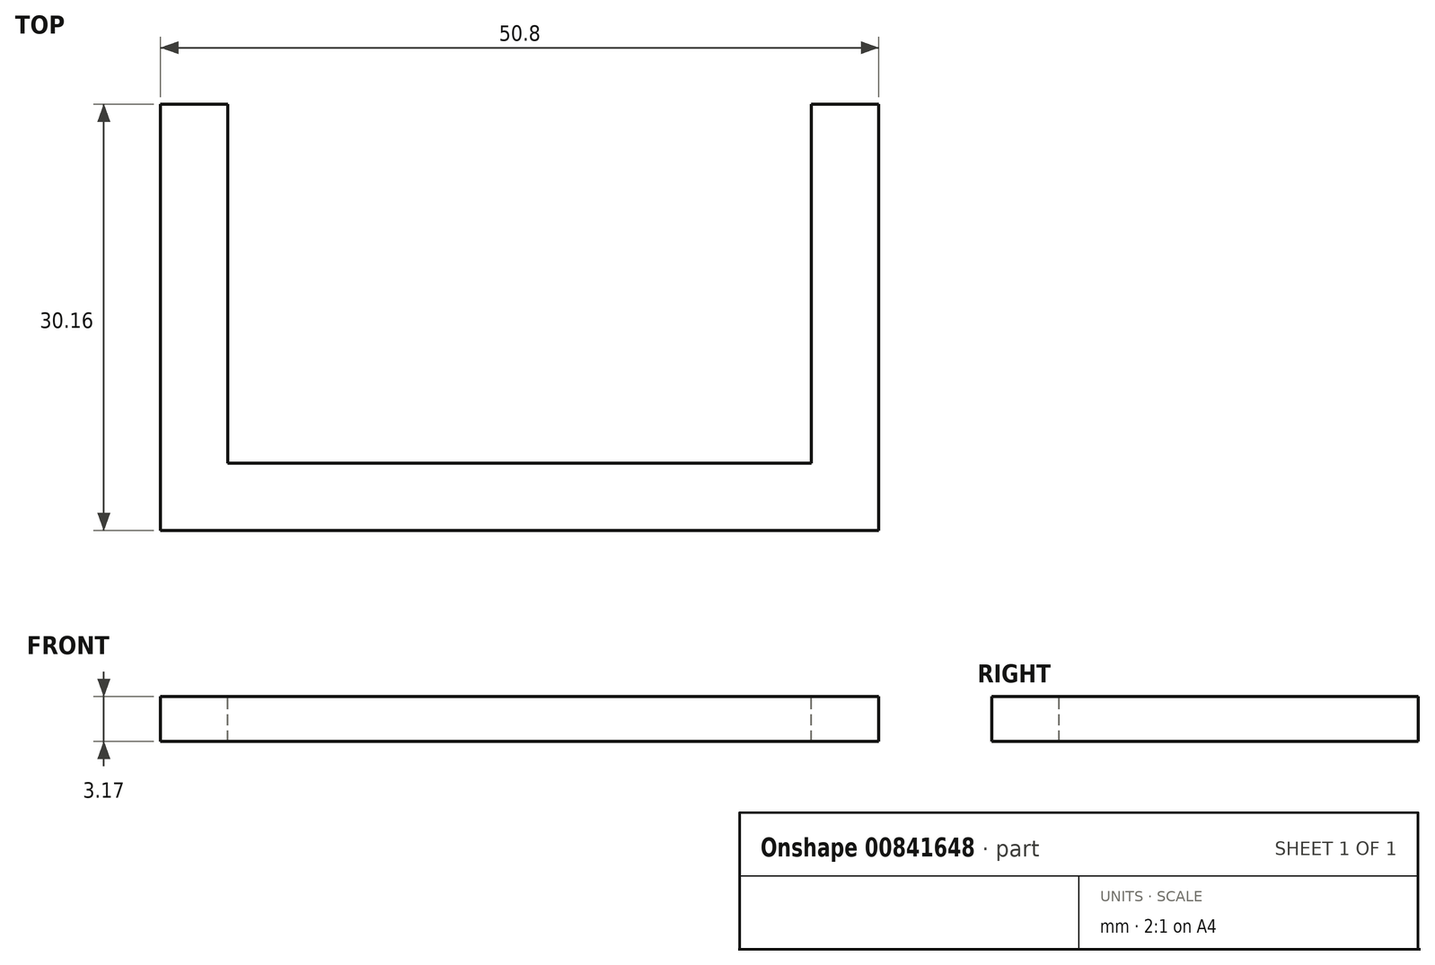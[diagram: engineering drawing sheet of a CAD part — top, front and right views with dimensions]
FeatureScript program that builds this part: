
annotation { "Feature Type Name" : "Feature", "Feature Type Description" : "" }
export const myFeature = defineFeature(function(context is Context, id is Id, definition is map)
    precondition{}
    {
        {
            var Q0;
            Q0=qCreatedBy(makeId("Top.planeOp"),FACE);
            var sketch = newSketch(context, id + "F0", { "sketchPlane" : qUnion([Q0])});
            skLineSegment(sketch, "E0.top", {"start": v(-34.87, -8.74) * mm, "end": v(6.4, -8.74) * mm});
            skLineSegment(sketch, "E0.left", {"start": v(-34.87, 16.66) * mm, "end": v(-34.87, -8.74) * mm});
            skLineSegment(sketch, "E0.right", {"start": v(6.4, 16.66) * mm, "end": v(6.4, -8.74) * mm});
            skLineSegment(sketch, "E1.top", {"start": v(-39.63, -13.5) * mm, "end": v(11.17, -13.5) * mm});
            skLineSegment(sketch, "E1.left", {"start": v(-39.63, 16.66) * mm, "end": v(-39.63, -13.5) * mm});
            skLineSegment(sketch, "E1.right", {"start": v(11.17, 16.66) * mm, "end": v(11.17, -13.5) * mm});
            skLineSegment(sketch, "E2", {"start": v(-39.63, 16.66) * mm, "end": v(-34.87, 16.66) * mm});
            skLineSegment(sketch, "E3", {"start": v(6.4, 16.66) * mm, "end": v(11.17, 16.66) * mm});
            skSolve(sketch);
        }
        {
            var Q0;
            Q0=makeQuery(id+"F0.imprint","IMPRINT",FACE,{"disambiguationData":[TD([[makeQuery(id+"F0.imprint","IMPRINT",EDGE,{"derivedFrom":sQuery(id+"F0.wireOp",EDGE,"E0.top")}),-1.0]])]});
            extrude(context, id + "F1", {"entities" : qUnion([Q0]), "oppositeDirection" : true, "depth" : 3.17 * mm, "offsetDistance" : 25.4 * mm});
        }
    });
